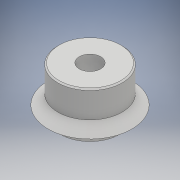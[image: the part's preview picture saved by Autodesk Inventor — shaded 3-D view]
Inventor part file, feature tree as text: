
AUTODESK INVENTOR PART (.ipt)
format: ipt  version: 2018 (Build 220112000, 112)  size: 129,024 bytes
history: native  units: mm
features: sketch x2, revolve x1, chamfer x1, extrude x1
ambient origin geometry x8: Origin, YZ Plane, XZ Plane, XY Plane, X Axis, Y Axis, Z Axis, Center Point
bodies: Solid1 (feature_tree)
feature tree (5):
  revolve  "Revolution1"  [1 undecoded]
  chamfer  "Chamfer1"  Distance=13.63mm
  extrude  "Extrusion1"  Depth=10.0mm
  sketch  "Sketch1"  dims[d0=12.0mm d1=10.0mm]
  sketch  "Sketch2"  dims[d2=15.63mm d3=13.63mm d4=17.61mm d5=6.0mm d6=9.515mm d7=16.0mm d8=90.0deg d9=0.5mm d10=2.0mm d11=45.0deg d12=8.0mm d13=10.0mm d14=0.0mm]
note: 1 required parameter value undecoded (feature->parameter linkage not recoverable at this tier; creation-order binding heuristic only, values carry confidence <= 0.55)
